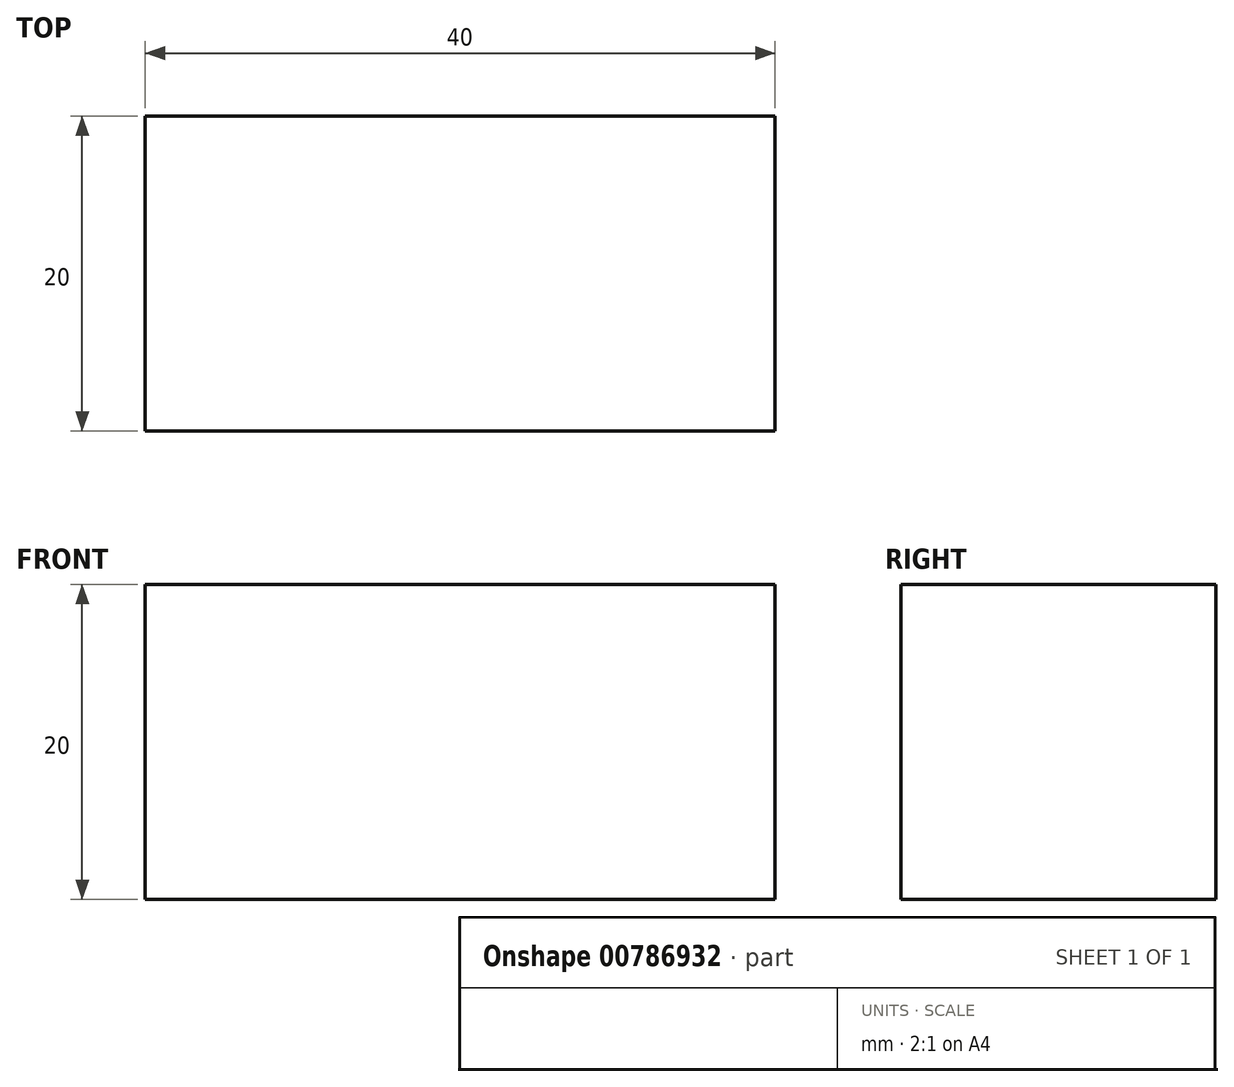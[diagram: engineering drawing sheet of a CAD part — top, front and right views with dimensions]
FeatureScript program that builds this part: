
annotation { "Feature Type Name" : "Feature", "Feature Type Description" : "" }
export const myFeature = defineFeature(function(context is Context, id is Id, definition is map)
    precondition{}
    {
        {
            var Q0;
            Q0=qCreatedBy(makeId("Top.planeOp"),FACE);
            var sketch = newSketch(context, id + "F0", { "sketchPlane" : qUnion([Q0])});
            skLineSegment(sketch, "E0.bottom", {"start": v(0, 0) * mm, "end": v(40, 0) * mm});
            skLineSegment(sketch, "E0.top", {"start": v(0, 20) * mm, "end": v(40, 20) * mm});
            skLineSegment(sketch, "E0.left", {"start": v(0, 0) * mm, "end": v(0, 20) * mm});
            skLineSegment(sketch, "E0.right", {"start": v(40, 0) * mm, "end": v(40, 20) * mm});
            skSolve(sketch);
        }
        {
            var Q0;
            Q0=makeQuery(id+"F0.imprint","IMPRINT",FACE,{"disambiguationData":[TD([[makeQuery(id+"F0.imprint","IMPRINT",EDGE,{"derivedFrom":sQuery(id+"F0.wireOp",EDGE,"E0.bottom")}),1.0]])]});
            extrude(context, id + "F1", {"entities" : qUnion([Q0]), "depth" : 20 * mm, "offsetDistance" : 25 * mm});
        }
        {
            var Q0;
            Q0=makeQuery(id+"F1.opExtrude","CAP_FACE",FACE,{"disambiguationData":[OSD([sQuery(id+"F0.wireOp",EDGE,"E0.bottom"),sQuery(id+"F0.wireOp",EDGE,"E0.top"),sQuery(id+"F0.wireOp",EDGE,"E0.left"),sQuery(id+"F0.wireOp",EDGE,"E0.right")])],"isStart":false});
            var sketch = newSketch(context, id + "F2", { "sketchPlane" : qUnion([Q0])});
            skLineSegment(sketch, "E1.bottom", {"start": v(2.5, 17.67) * mm, "end": v(37.12, 17.67) * mm});
            skLineSegment(sketch, "E1.top", {"start": v(2.5, 2.96) * mm, "end": v(37.12, 2.96) * mm});
            skLineSegment(sketch, "E1.left", {"start": v(2.5, 17.67) * mm, "end": v(2.5, 2.96) * mm});
            skLineSegment(sketch, "E1.right", {"start": v(37.12, 17.67) * mm, "end": v(37.12, 2.96) * mm});
            skSolve(sketch);
        }
        {
            var Q0;
            Q0 = qSketchRegion(id + "F2", true);
            extrude(context, id + "F3", {"entities" : qUnion([Q0]), "operationType" : NewBodyOperationType.ADD, "oppositeDirection" : true, "depth" : 15 * mm, "offsetDistance" : 25 * mm});
        }
    });
